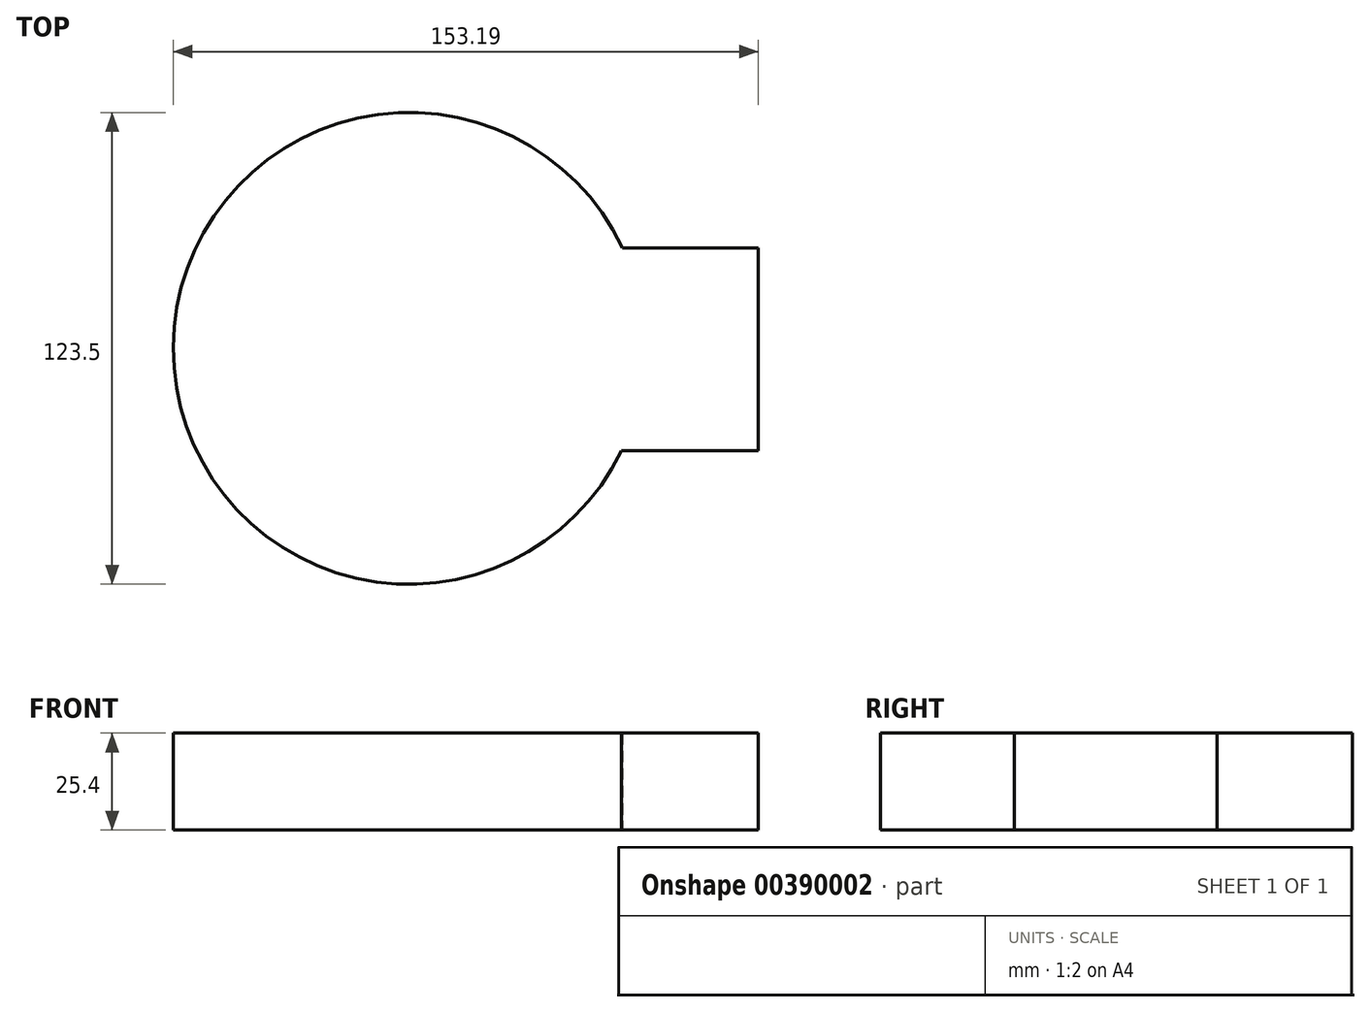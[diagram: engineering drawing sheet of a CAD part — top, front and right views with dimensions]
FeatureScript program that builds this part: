
annotation { "Feature Type Name" : "Feature", "Feature Type Description" : "" }
export const myFeature = defineFeature(function(context is Context, id is Id, definition is map)
    precondition{}
    {
        {
            var Q0;
            Q0=qCreatedBy(makeId("Top.planeOp"),FACE);
            var sketch = newSketch(context, id + "F0", { "sketchPlane" : qUnion([Q0])});
            skArc(sketch, "E0", {"start": v(55.85, 26.33) * mm, "mid": v(-61.75, 0.24) * mm, "end": v(55.65, -26.75) * mm});
            skLineSegment(sketch, "E1.bottom", {"start": v(55.85, 26.33) * mm, "end": v(91.44, 26.33) * mm});
            skLineSegment(sketch, "E1.top", {"start": v(55.65, -26.75) * mm, "end": v(91.44, -26.75) * mm});
            skLineSegment(sketch, "E1.right", {"start": v(91.44, 26.33) * mm, "end": v(91.44, -26.75) * mm});
            skSolve(sketch);
        }
        {
            var Q0;
            Q0 = qSketchRegion(id + "F0", true);
            extrude(context, id + "F1", {"entities" : qUnion([Q0]), "depth" : 25.4 * mm});
        }
    });
